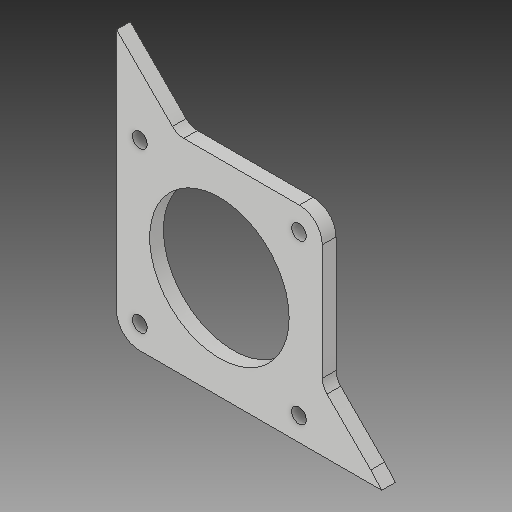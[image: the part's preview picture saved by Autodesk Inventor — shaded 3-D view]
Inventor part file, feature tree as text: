
AUTODESK INVENTOR PART (.ipt)
format: ipt  version: 2018 (Build 220112000, 112)  size: 142,336 bytes
history: native  units: mm
features: extrude x4, sketch x4, reference x4, fillet x1
ambient origin geometry x8: Origin, YZ Plane, XZ Plane, XY Plane, X Axis, Y Axis, Z Axis, Center Point
bodies: Solid1 (feature_tree)
feature tree (13):
  extrude  "Extrusion1"  Depth=90.0mm
  extrude  "Extrusion2"  Depth=6.0mm TaperAngle=0.0deg
  extrude  "Extrusion3"  Depth=6.0mm TaperAngle=0.0deg
  fillet  "Fillet1"  Radius=6.0mm
  extrude  "Extrusion4"  Depth=7.0mm
  sketch  "Sketch1"  dims[d0=90.0mm d1=90.0mm]
  sketch  "Sketch2"  dims[d2=10.0mm d3=6.0mm d4=0.0mm]
  sketch  "Sketch3"  dims[d5=61.0mm d6=6.0mm d7=0.0mm d9=6.0mm d10=0.0mm]
  sketch  "Sketch4"  dims[d13=53.5mm d15=7.0mm d16=10.0mm d17=0.0mm]
  reference  "Reference1"
  reference  "Reference2"
  reference  "Reference3"
  reference  "Reference4"
